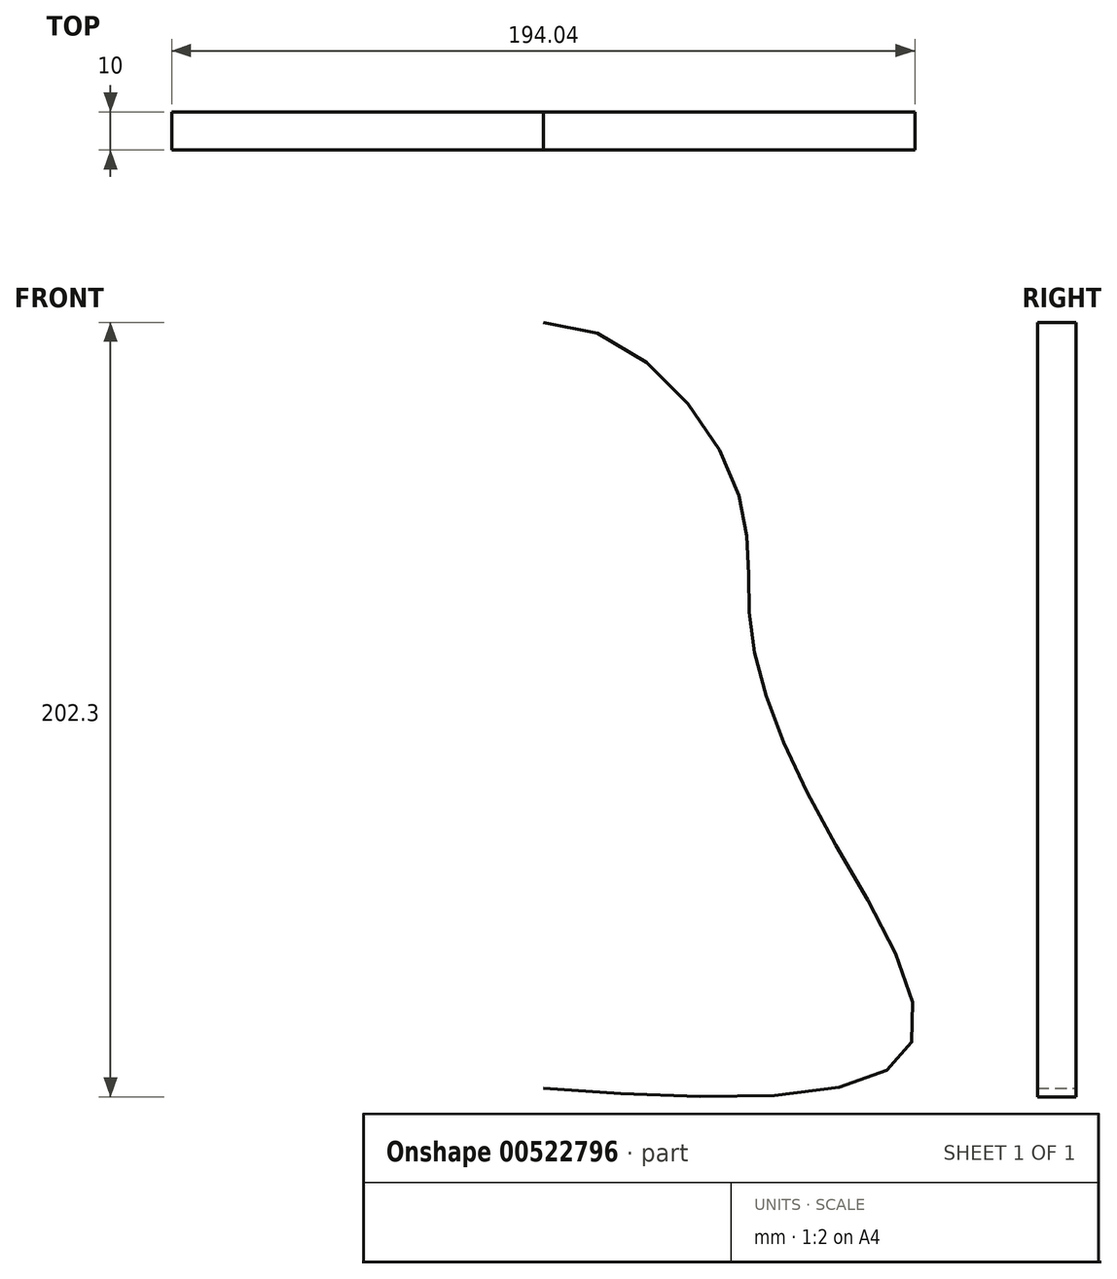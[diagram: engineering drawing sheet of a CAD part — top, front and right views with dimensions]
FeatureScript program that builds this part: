
annotation { "Feature Type Name" : "Feature", "Feature Type Description" : "" }
export const myFeature = defineFeature(function(context is Context, id is Id, definition is map)
    precondition{}
    {
        {
            var Q0;
            Q0=qCreatedBy(makeId("Front.planeOp"),FACE);
            var sketch = newSketch(context, id + "F0", { "sketchPlane" : qUnion([Q0])});
            skFitSpline(sketch, "E0", {"points": [v(0, 116.67) * mm, v(-50, 74.6) * mm, v(-53.97, 38.36) * mm, v(-73.8, -15.34) * mm, v(-95, -73.8) * mm, v(0, -83.33) * mm], "startDerivative": vector(-336.63, 3.89) * mm, "endDerivative": vector(447.44, 33.77) * mm});
            skLineSegment(sketch, "E1", {"start": v(0, 116.67) * mm, "end": v(0, -83.33) * mm, "construction": true});
            skFitSpline(sketch, "E2.MirrorCS", {"points": [v(0, 116.67) * mm, v(50, 74.6) * mm, v(53.97, 38.36) * mm, v(73.8, -15.34) * mm, v(95, -73.8) * mm, v(0, -83.33) * mm], "startDerivative": vector(336.63, 3.89) * mm, "endDerivative": vector(-447.44, 33.77) * mm});
            skSolve(sketch);
        }
        {
            var Q0;
            Q0 = qSketchRegion(id + "F0", true);
            extrude(context, id + "F1", {"entities" : qUnion([Q0]), "depth" : 10 * mm, "offsetDistance" : 25 * mm});
        }
    });
